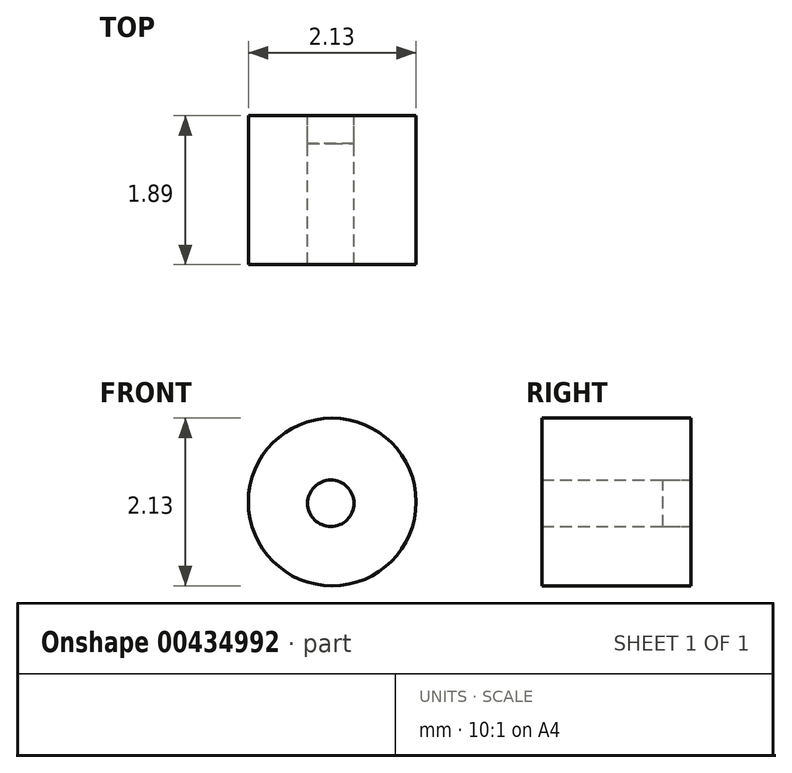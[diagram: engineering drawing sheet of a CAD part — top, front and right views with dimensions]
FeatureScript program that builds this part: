
annotation { "Feature Type Name" : "Feature", "Feature Type Description" : "" }
export const myFeature = defineFeature(function(context is Context, id is Id, definition is map)
    precondition{}
    {
        {
            var Q0;
            Q0=qCreatedBy(makeId("Front.planeOp"),FACE);
            var sketch = newSketch(context, id + "F0", { "sketchPlane" : qUnion([Q0])});
            skCircle(sketch, "E0", {"center": v(-35.3, 9.98) * mm, "radius": 1.06 * mm});
            skSolve(sketch);
        }
        {
            var Q0;
            Q0=makeQuery(id+"F0.imprint","IMPRINT",FACE,{"disambiguationData":[TD([[makeQuery(id+"F0.imprint","IMPRINT",EDGE,{"derivedFrom":sQuery(id+"F0.wireOp",EDGE,"E0")}),1.0]])]});
            var sketch = newSketch(context, id + "F1", { "sketchPlane" : qUnion([Q0])});
            skCircle(sketch, "E1", {"center": v(-35.31, 9.97) * mm, "radius": 0.3 * mm});
            skSolve(sketch);
        }
        {
            var Q0;
            Q0 = qSketchRegion(id + "F1", true);
            var Q1;
            Q1=makeQuery(id+"F0.imprint","IMPRINT",FACE,{"disambiguationData":[TD([[makeQuery(id+"F0.imprint","IMPRINT",EDGE,{"derivedFrom":sQuery(id+"F0.wireOp",EDGE,"E0")}),1.0]])]});
            extrude(context, id + "F2", {"entities" : qUnion([Q0, Q1]), "depth" : 1.89 * mm});
        }
        {
            var Q0;
            Q0 = qSketchRegion(id + "F1", true);
            extrude(context, id + "F3", {"entities" : qUnion([Q0]), "depth" : 0.35 * mm});
        }
    });
